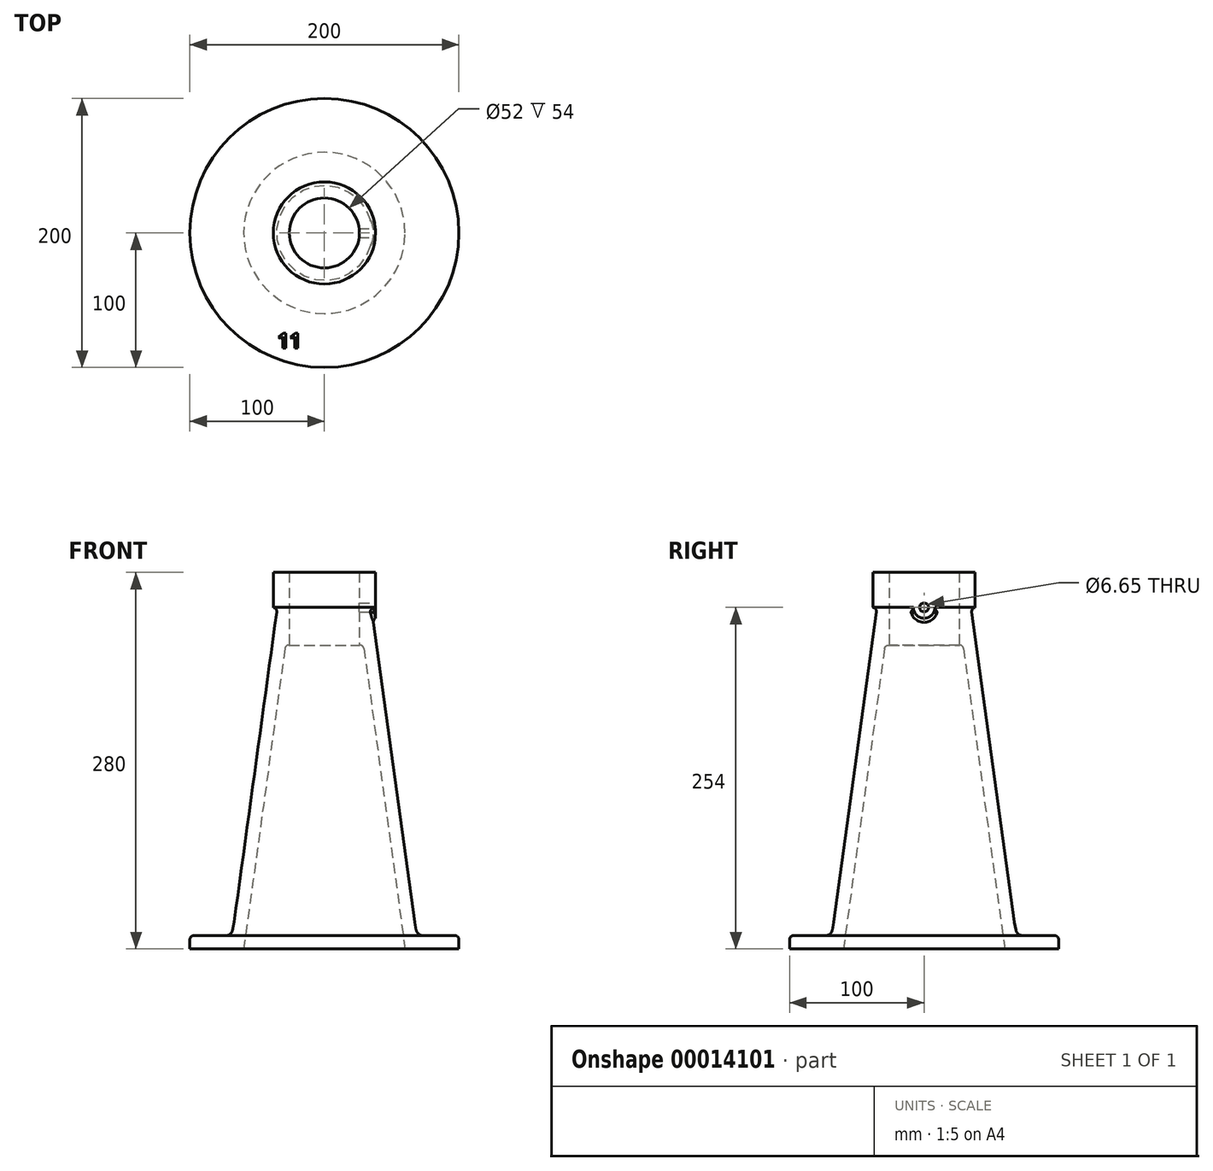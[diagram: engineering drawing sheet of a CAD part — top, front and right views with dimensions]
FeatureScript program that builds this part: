
annotation { "Feature Type Name" : "Feature", "Feature Type Description" : "" }
export const myFeature = defineFeature(function(context is Context, id is Id, definition is map)
    precondition{}
    {
        {
            var Q0;
            Q0=qCreatedBy(makeId("Front.planeOp"),FACE);
            var sketch = newSketch(context, id + "F0", { "sketchPlane" : qUnion([Q0])});
            skLineSegment(sketch, "E0", {"start": v(0, 0) * mm, "end": v(0, 55.8) * mm, "construction": true});
            skLineSegment(sketch, "E1", {"start": v(60, 0) * mm, "end": v(100, 0) * mm});
            skLineSegment(sketch, "E2", {"start": v(100, 0) * mm, "end": v(100, 10) * mm});
            skLineSegment(sketch, "E3", {"start": v(100, 10) * mm, "end": v(69.1, 10) * mm});
            skLineSegment(sketch, "E4", {"start": v(69.1, 10) * mm, "end": v(67.1, 20) * mm});
            skLineSegment(sketch, "E5", {"start": v(67.1, 20) * mm, "end": v(35, 254) * mm});
            skLineSegment(sketch, "E6", {"start": v(35, 254) * mm, "end": v(38, 254) * mm});
            skLineSegment(sketch, "E7", {"start": v(38, 254) * mm, "end": v(38, 280) * mm});
            skLineSegment(sketch, "E8", {"start": v(38, 280) * mm, "end": v(26, 280) * mm});
            skLineSegment(sketch, "E9", {"start": v(26, 280) * mm, "end": v(26, 226) * mm});
            skLineSegment(sketch, "E10", {"start": v(26, 226) * mm, "end": v(29, 226) * mm});
            skLineSegment(sketch, "E11", {"start": v(29, 226) * mm, "end": v(60, 0) * mm});
            skSolve(sketch);
        }
        {
            var Q0;
            Q0=makeQuery(id+"F0.imprint","IMPRINT",FACE,{"disambiguationData":[TD([[makeQuery(id+"F0.imprint","IMPRINT",EDGE,{"derivedFrom":sQuery(id+"F0.wireOp",EDGE,"E1")}),1.0]])]});
            var Q1;
            Q1=sQuery(id+"F0.wireOp",EDGE,"E0");
            revolve(context, id + "F1", {"entities" : qUnion([Q0]), "axis" : qUnion([Q1]), "revolveType" : RevolveType.FULL});
        }
        {
            var Q0;
            Q0=qCreatedBy(makeId("Right.planeOp"),FACE);
            cPlane(context, id + "F2", {"entities" : qUnion([Q0]), "cplaneType" : CPlaneType.OFFSET, "offset" : 38 * mm, "width" : 150 * mm, "height" : 150 * mm});
        }
        {
            var Q0;
            Q0=qCreatedBy(id+"F2.planeOp",FACE);
            var sketch = newSketch(context, id + "F3", { "sketchPlane" : qUnion([Q0])});
            skLineSegment(sketch, "E12.0", {"start": v(38, 254) * mm, "end": v(-38, 254) * mm});
            skArc(sketch, "E13", {"start": v(-8, 254) * mm, "mid": v(0, 246) * mm, "end": v(8, 254) * mm});
            skSolve(sketch);
        }
        {
            var Q0;
            {var subQ0=sQuery(id+"F3.wireOp",EDGE,"E13");Q0=makeQuery(id+"F3.imprint","IMPRINT",FACE,{"disambiguationData":[TD([[makeQuery(id+"F3.imprint","IMPRINT",EDGE,{"derivedFrom":subQ0}),1.0]])]});}
            extrude(context, id + "F4", {"entities" : qUnion([Q0]), "operationType" : NewBodyOperationType.ADD, "oppositeDirection" : true, "depth" : 5 * mm});
        }
        {
            var Q0;
            Q0=makeQuery(id+"F1.opRevolve","SWEPT_FACE",FACE,{"disambiguationData":[OSD([sQuery(id+"F0.wireOp",EDGE,"E8")])]});
            var sketch = newSketch(context, id + "F5", { "sketchPlane" : qUnion([Q0])});
            skCircle(sketch, "E14.0", {"center": v(0, 0) * mm, "radius": 38 * mm});
            skLineSegment(sketch, "E15", {"start": v(33.48, 17.98) * mm, "end": v(56.5, 17.98) * mm});
            skLineSegment(sketch, "E16", {"start": v(56.5, 17.98) * mm, "end": v(56.5, -15.06) * mm});
            skLineSegment(sketch, "E17", {"start": v(56.5, -15.06) * mm, "end": v(31.68, -20.99) * mm});
            skSolve(sketch);
        }
        {
            var Q0;
            {var subQ1=sQuery(id+"F5.wireOp",EDGE,"E15");Q0=makeQuery(id+"F5.imprint","IMPRINT",FACE,{"disambiguationData":[TD([[makeQuery(id+"F5.imprint","IMPRINT",EDGE,{"derivedFrom":subQ1}),-1.0]])]});}
            extrude(context, id + "F6", {"entities" : qUnion([Q0]), "operationType" : NewBodyOperationType.REMOVE, "oppositeDirection" : true, "depth" : 35 * mm});
        }
        {
            var Q0;
            Q0=qCreatedBy(id+"F2.planeOp",FACE);
            var sketch = newSketch(context, id + "F7", { "sketchPlane" : qUnion([Q0])});
            skArc(sketch, "E18.0", {"start": v(-8, 254) * mm, "mid": v(0, 246) * mm, "end": v(8, 254) * mm});
            skCircle(sketch, "E19", {"center": v(0, 254) * mm, "radius": 3.33 * mm});
            skSolve(sketch);
        }
        {
            var Q0;
            Q0=makeQuery(id+"F7.imprint","IMPRINT",FACE,{"disambiguationData":[TD([[makeQuery(id+"F7.imprint","IMPRINT",EDGE,{"derivedFrom":sQuery(id+"F7.wireOp",EDGE,"E19")}),1.0]])]});
            extrude(context, id + "F8", {"entities" : qUnion([Q0]), "operationType" : NewBodyOperationType.REMOVE, "oppositeDirection" : true, "depth" : 25 * mm});
        }
        {
            var Q0;
            Q0=makeQuery(id+"F1.opRevolve","SWEPT_EDGE",EDGE,{"disambiguationData":[OSD([sQuery(id+"F0.wireOp",EDGE,"E3"),sQuery(id+"F0.wireOp",EDGE,"E4")])]});
            var Q1;
            Q1=makeQuery(id+"F1.opRevolve","SWEPT_EDGE",EDGE,{"disambiguationData":[OSD([sQuery(id+"F0.wireOp",EDGE,"E4"),sQuery(id+"F0.wireOp",EDGE,"E5")])]});
            var Q2;
            {var subQ0=sQuery(id+"F3.wireOp",EDGE,"E12.0");var subQ1=sQuery(id+"F3.wireOp",EDGE,"E13");Q2=makeQuery(id+"F4.boolean.opBoolean","SPLIT",EDGE,{"disambiguationData":[TD([makeQuery(id+"F1.opRevolve","SWEPT_FACE",FACE,{"disambiguationData":[OSD([sQuery(id+"F0.wireOp",EDGE,"E5")])]})])],"derivedFrom":makeQuery(id+"F4.opExtrude","SWEPT_EDGE",EDGE,{"disambiguationData":[OSD([subQ0,subQ1]),TDD([makeQuery(id+"F3.imprint","INTERSECT",VERTEX,{"disambiguationData":[OD(0.0)],"derivedFrom":[subQ0,subQ1]})])]})});}
            var Q3;
            {var subQ0=sQuery(id+"F3.wireOp",EDGE,"E12.0");var subQ1=sQuery(id+"F3.wireOp",EDGE,"E13");Q3=makeQuery(id+"F4.boolean.opBoolean","SPLIT",EDGE,{"disambiguationData":[TD([makeQuery(id+"F1.opRevolve","SWEPT_FACE",FACE,{"disambiguationData":[OSD([sQuery(id+"F0.wireOp",EDGE,"E5")])]})])],"derivedFrom":makeQuery(id+"F4.opExtrude","SWEPT_EDGE",EDGE,{"disambiguationData":[OSD([subQ0,subQ1]),TDD([makeQuery(id+"F3.imprint","INTERSECT",VERTEX,{"disambiguationData":[OD(1.0)],"derivedFrom":[subQ0,subQ1]})])]})});}
            fillet(context, id + "F9", {"entities" : qUnion([Q0, Q1, Q2, Q3]), "radius" : 5 * mm, "tangentPropagation" : true, "allowEdgeOverflow" : false});
        }
        {
            var Q0;
            Q0=makeQuery(id+"F1.opRevolve","SWEPT_FACE",FACE,{"disambiguationData":[OSD([sQuery(id+"F0.wireOp",EDGE,"E5")])]});
            var Q1;
            Q1=makeQuery(id+"F1.opRevolve","SWEPT_EDGE",EDGE,{"disambiguationData":[OSD([sQuery(id+"F0.wireOp",EDGE,"E10"),sQuery(id+"F0.wireOp",EDGE,"E11")])]});
            var Q2;
            Q2=makeQuery(id+"F1.opRevolve","SWEPT_EDGE",EDGE,{"disambiguationData":[OSD([sQuery(id+"F0.wireOp",EDGE,"E2"),sQuery(id+"F0.wireOp",EDGE,"E3")])]});
            fillet(context, id + "F10", {"entities" : qUnion([Q0, Q1, Q2]), "radius" : 3 * mm, "tangentPropagation" : true, "allowEdgeOverflow" : false});
        }
        {
            var Q0;
            Q0=makeQuery(id+"F1.opRevolve","SWEPT_FACE",FACE,{"disambiguationData":[OSD([sQuery(id+"F0.wireOp",EDGE,"E3")])]});
            var sketch = newSketch(context, id + "F11", { "sketchPlane" : qUnion([Q0])});
            skText(sketch, "E20", { "text": "11", "fontName": "OpenSans-Bold.ttf"});
            const initialGuessF11  = {"E20": [-0.03491, -0.08555, 1, 0, 0.01105]};
            skSetInitialGuess(sketch, initialGuessF11);
            skSolve(sketch);
        }
        {
            var Q0;
            Q0 = qSketchRegion(id + "F11", true);
            extrude(context, id + "F12", {"entities" : qUnion([Q0]), "operationType" : NewBodyOperationType.REMOVE, "oppositeDirection" : true, "depth" : .5 * mm});
        }
    });
